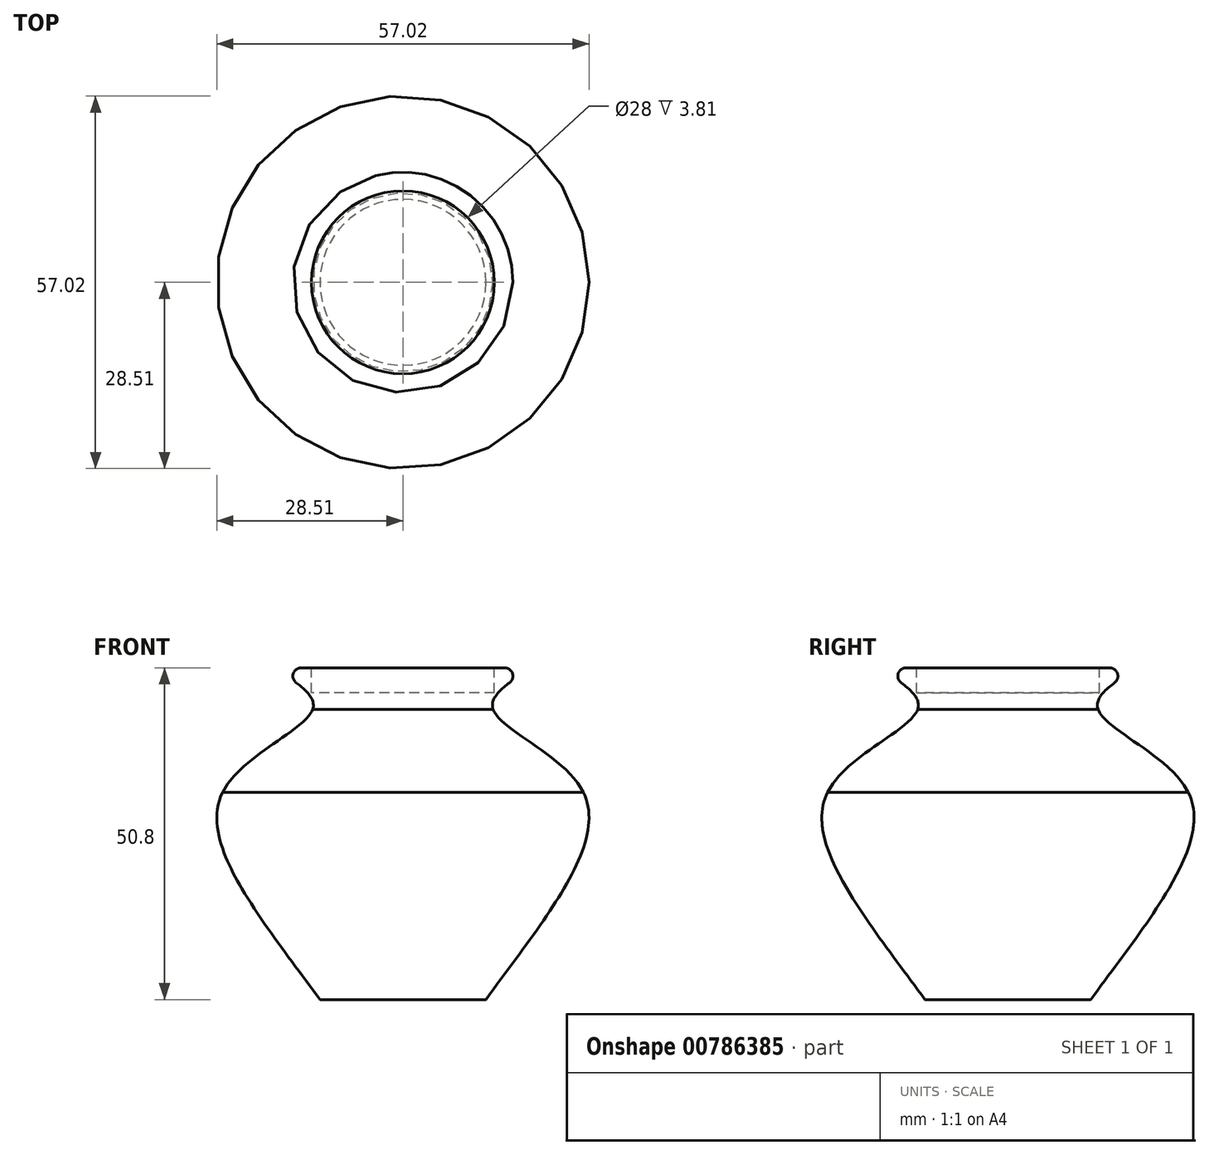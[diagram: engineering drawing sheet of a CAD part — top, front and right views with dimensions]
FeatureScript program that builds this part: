
annotation { "Feature Type Name" : "Feature", "Feature Type Description" : "" }
export const myFeature = defineFeature(function(context is Context, id is Id, definition is map)
    precondition{}
    {
        {
            var Q0;
            Q0=qCreatedBy(makeId("Front.planeOp"),FACE);
            var sketch = newSketch(context, id + "F0", { "sketchPlane" : qUnion([Q0])});
            skLineSegment(sketch, "E0", {"start": v(0, -31.75) * mm, "end": v(12.7, -31.75) * mm});
            skLineSegment(sketch, "E1", {"start": v(0, 0) * mm, "end": v(0, -31.75) * mm});
            skLineSegment(sketch, "E2", {"start": v(0, 0) * mm, "end": v(27.63, 0) * mm});
            skLineSegment(sketch, "E3", {"start": v(0, 0) * mm, "end": v(0, 12.7) * mm});
            skLineSegment(sketch, "E4", {"start": v(0, 12.7) * mm, "end": v(13.81, 12.7) * mm});
            skFitSpline(sketch, "E5", {"points": [v(12.7, -31.75) * mm, v(27.63, 0) * mm, v(13.81, 12.7) * mm, v(19.85, 19.05) * mm], "startDerivative": vector(62.73, 85.62) * mm, "endDerivative": vector(45.71, 28.77) * mm});
            skLineSegment(sketch, "E6", {"start": v(19.85, 19.05) * mm, "end": v(0, 19.05) * mm});
            skLineSegment(sketch, "E7", {"start": v(0, 19.05) * mm, "end": v(0, 12.7) * mm});
            skFitSpline(sketch, "E8.MirrorCS", {"points": [v(-12.7, -31.75) * mm, v(-27.63, 0) * mm, v(-13.81, 12.7) * mm, v(-19.85, 19.05) * mm], "startDerivative": vector(-62.73, 85.62) * mm, "endDerivative": vector(-45.71, 28.77) * mm});
            skLineSegment(sketch, "E9", {"start": v(-19.85, 19.05) * mm, "end": v(0, 19.05) * mm});
            skLineSegment(sketch, "E10", {"start": v(-27.63, 0) * mm, "end": v(0, 0) * mm});
            skLineSegment(sketch, "E11", {"start": v(-13.81, 12.7) * mm, "end": v(0, 12.7) * mm});
            skLineSegment(sketch, "E12", {"start": v(-12.7, -31.75) * mm, "end": v(0, -31.75) * mm});
            skLineSegment(sketch, "E13", {"start": v(0, -14.76) * mm, "end": v(-24.67, -14.76) * mm});
            skLineSegment(sketch, "E14", {"start": v(0, -14.76) * mm, "end": v(24.67, -14.76) * mm});
            skSolve(sketch);
        }
        {
            var Q0;
            {var subQ0=sQuery(id+"F0.wireOp",EDGE,"E4");Q0=makeQuery(id+"F0.imprint","IMPRINT",FACE,{"disambiguationData":[TD([[makeQuery(id+"F0.imprint","IMPRINT",EDGE,{"derivedFrom":subQ0}),1.0]])]});}
            var Q1;
            {var subQ0=sQuery(id+"F0.wireOp",EDGE,"E2");Q1=makeQuery(id+"F0.imprint","IMPRINT",FACE,{"disambiguationData":[TD([[makeQuery(id+"F0.imprint","IMPRINT",EDGE,{"derivedFrom":subQ0}),1.0]])]});}
            var Q2;
            {var subQ0=sQuery(id+"F0.wireOp",EDGE,"E2");Q2=makeQuery(id+"F0.imprint","IMPRINT",FACE,{"disambiguationData":[TD([[makeQuery(id+"F0.imprint","IMPRINT",EDGE,{"derivedFrom":subQ0}),-1.0]])]});}
            var Q3;
            {var subQ0=sQuery(id+"F0.wireOp",EDGE,"E0");Q3=makeQuery(id+"F0.imprint","IMPRINT",FACE,{"disambiguationData":[TD([[makeQuery(id+"F0.imprint","IMPRINT",EDGE,{"derivedFrom":subQ0}),1.0]])]});}
            var Q4;
            Q4=sQuery(id+"F0.wireOp",EDGE,"E7");
            revolve(context, id + "F1", {"surfaceOperationType" : NewSurfaceOperationType.NEW, "entities" : qUnion([Q0, Q1, Q2, Q3]), "axis" : qUnion([Q4]), "revolveType" : RevolveType.FULL});
        }
        {
            var Q0;
            Q0=makeQuery(id+"F1.opRevolve","SWEPT_EDGE",EDGE,{"disambiguationData":[OSD([sQuery(id+"F0.wireOp",EDGE,"E5"),sQuery(id+"F0.wireOp",EDGE,"E6")])]});
            fillet(context, id + "F2", {"entities" : qUnion([Q0]), "radius" : 1.27 * mm, "tangentPropagation" : true, "allowEdgeOverflow" : false});
        }
        {
            var Q0;
            Q0=makeQuery(id+"F1.opRevolve","SWEPT_FACE",FACE,{"disambiguationData":[OSD([sQuery(id+"F0.wireOp",EDGE,"E6")])]});
            var sketch = newSketch(context, id + "F3", { "sketchPlane" : qUnion([Q0])});
            skCircle(sketch, "E15", {"center": v(0, 0) * mm, "radius": 14 * mm});
            skSolve(sketch);
        }
        {
            var Q0;
            Q0=makeQuery(id+"F3.imprint","IMPRINT",FACE,{"disambiguationData":[TD([[makeQuery(id+"F3.imprint","IMPRINT",EDGE,{"derivedFrom":sQuery(id+"F3.wireOp",EDGE,"E15")}),1.0]])]});
            extrude(context, id + "F4", {"entities" : qUnion([Q0]), "operationType" : NewBodyOperationType.REMOVE, "oppositeDirection" : true, "depth" : 3.8 * mm, "offsetDistance" : 25.4 * mm});
        }
    });
